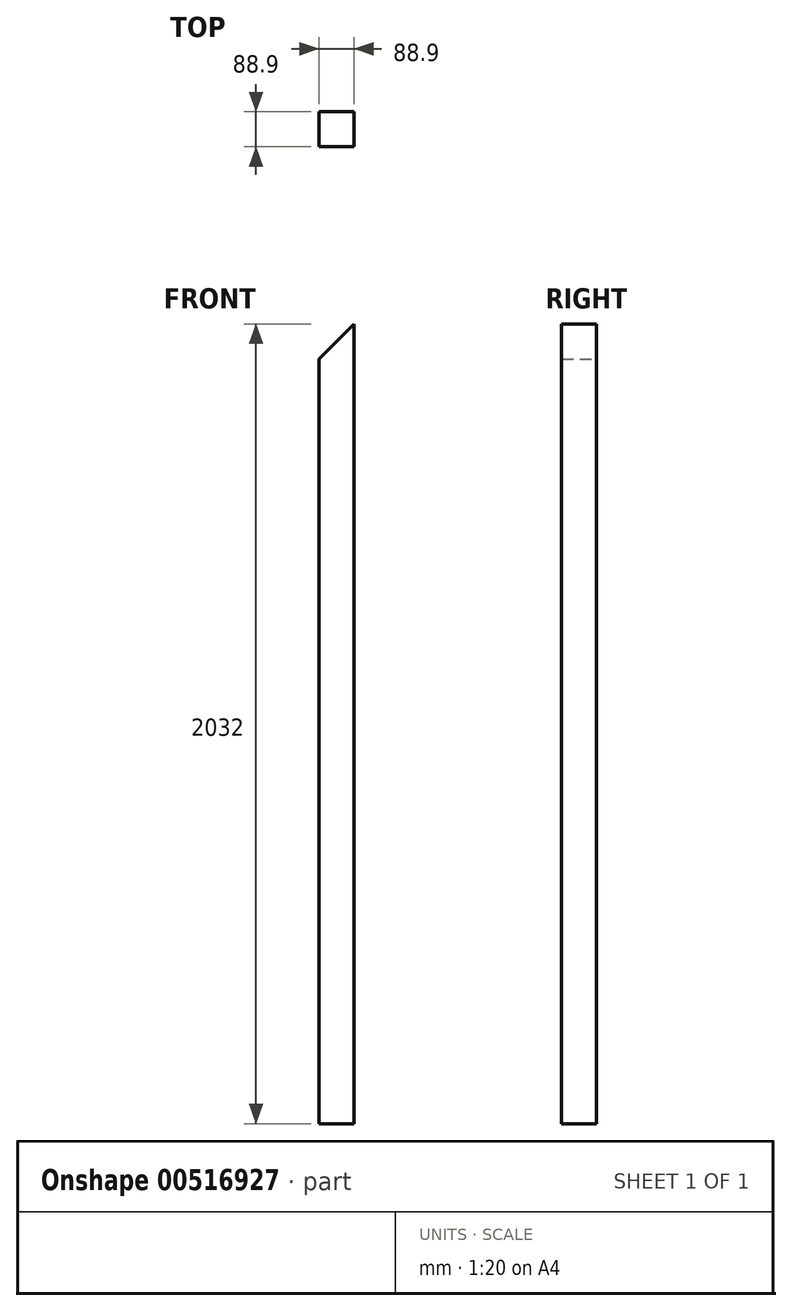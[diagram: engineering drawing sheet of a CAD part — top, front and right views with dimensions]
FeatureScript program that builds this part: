
annotation { "Feature Type Name" : "Feature", "Feature Type Description" : "" }
export const myFeature = defineFeature(function(context is Context, id is Id, definition is map)
    precondition{}
    {
        {
            var Q0;
            Q0=qCreatedBy(makeId("Front.planeOp"),FACE);
            var sketch = newSketch(context, id + "F0", { "sketchPlane" : qUnion([Q0])});
            skLineSegment(sketch, "E0", {"start": v(0, 0) * mm, "end": v(0, 1943.1) * mm});
            skLineSegment(sketch, "E1", {"start": v(0, 1943.1) * mm, "end": v(88.9, 2032) * mm});
            skLineSegment(sketch, "E2", {"start": v(88.9, 2032) * mm, "end": v(88.9, 0) * mm});
            skLineSegment(sketch, "E3", {"start": v(88.9, 0) * mm, "end": v(0, 0) * mm});
            skSolve(sketch);
        }
        {
            var Q0;
            Q0 = qSketchRegion(id + "F0", true);
            extrude(context, id + "F1", {"entities" : qUnion([Q0]), "depth" : 88.9 * mm, "offsetDistance" : 25.4 * mm});
        }
    });
